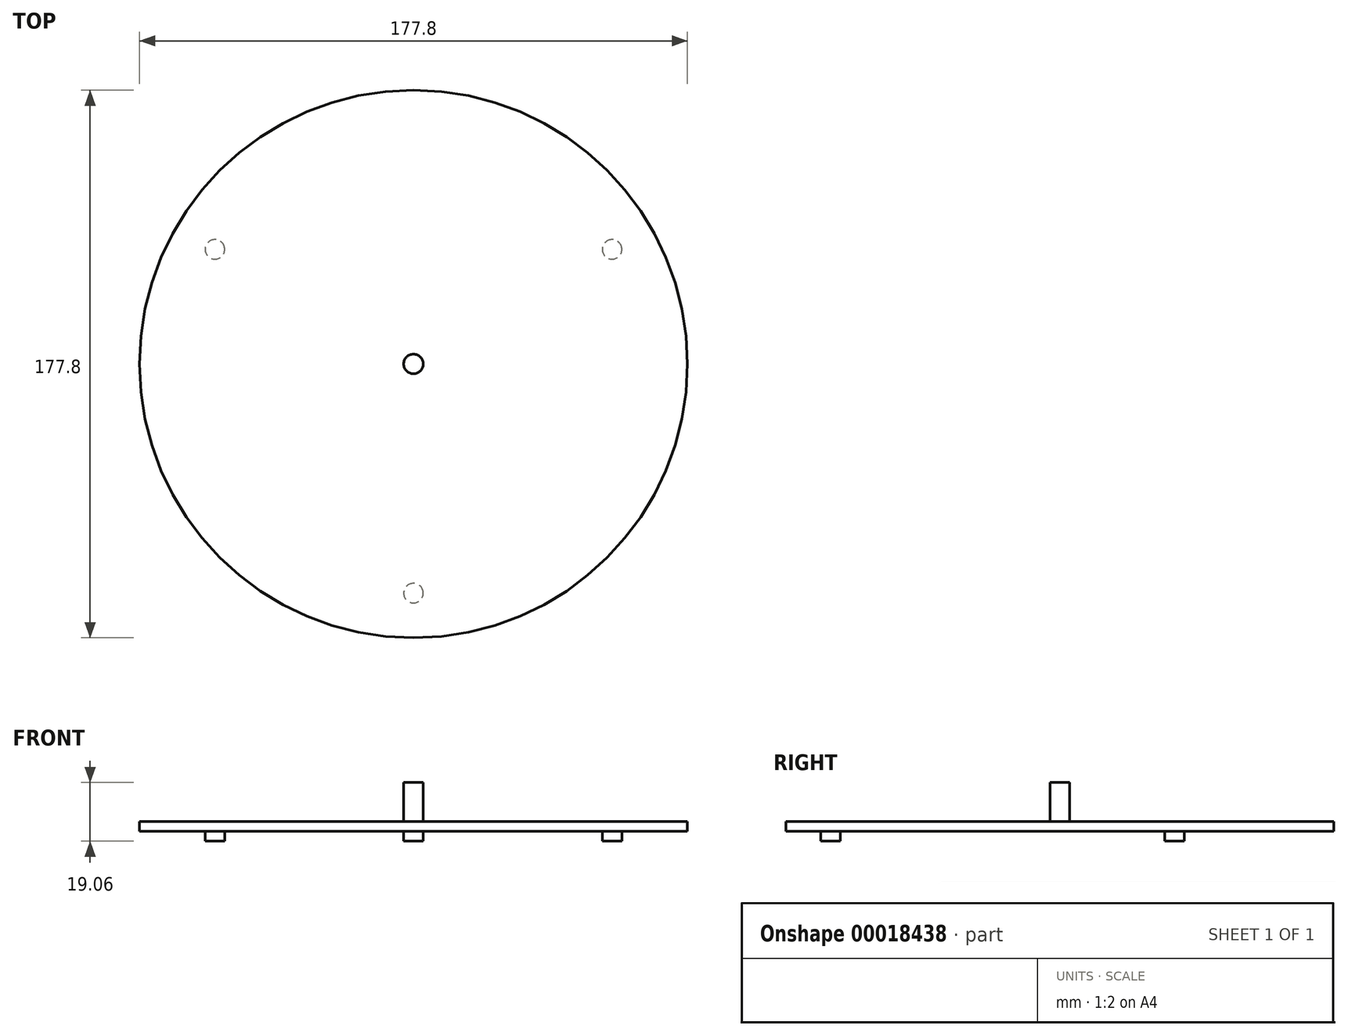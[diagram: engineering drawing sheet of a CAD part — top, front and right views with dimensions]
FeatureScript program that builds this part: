
annotation { "Feature Type Name" : "Feature", "Feature Type Description" : "" }
export const myFeature = defineFeature(function(context is Context, id is Id, definition is map)
    precondition{}
    {
        {
            var Q0;
            Q0=qCreatedBy(makeId("Top.planeOp"),FACE);
            var sketch = newSketch(context, id + "F0", { "sketchPlane" : qUnion([Q0])});
            skCircle(sketch, "E0", {"center": v(0, 0) * mm, "radius": 88.9 * mm});
            skSolve(sketch);
        }
        {
            var Q0;
            Q0=makeQuery(id+"F0.imprint","IMPRINT",FACE,{"disambiguationData":[TD([[makeQuery(id+"F0.imprint","IMPRINT",EDGE,{"derivedFrom":sQuery(id+"F0.wireOp",EDGE,"E0")}),1.0]])]});
            extrude(context, id + "F1", {"entities" : qUnion([Q0]), "depth" : 3.17 * mm});
        }
        {
            var Q0;
            Q0=makeQuery(id+"F1.opExtrude","CAP_FACE",FACE,{"disambiguationData":[OSD([sQuery(id+"F0.wireOp",EDGE,"E0")])],"isStart":false});
            var sketch = newSketch(context, id + "F2", { "sketchPlane" : qUnion([Q0])});
            skCircle(sketch, "E1", {"center": v(0, 0) * mm, "radius": 3.18 * mm});
            skSolve(sketch);
        }
        {
            var Q0;
            Q0=makeQuery(id+"F2.imprint","IMPRINT",FACE,{"disambiguationData":[TD([[makeQuery(id+"F2.imprint","IMPRINT",EDGE,{"derivedFrom":sQuery(id+"F2.wireOp",EDGE,"E1")}),1.0]])]});
            extrude(context, id + "F3", {"entities" : qUnion([Q0]), "operationType" : NewBodyOperationType.ADD, "depth" : 12.7 * mm});
        }
        {
            var Q0;
            Q0=makeQuery(id+"F1.opExtrude","CAP_FACE",FACE,{"disambiguationData":[OSD([sQuery(id+"F0.wireOp",EDGE,"E0")])],"isStart":false});
            var sketch = newSketch(context, id + "F4", { "sketchPlane" : qUnion([Q0])});
            skCircle(sketch, "E2.cCircle", {"center": v(0, 0) * mm, "radius": 74.4 * mm, "construction": true});
            skLineSegment(sketch, "E2.0", {"start": v(64.44, 37.2) * mm, "end": v(0, -74.4) * mm});
            skLineSegment(sketch, "E2.1", {"start": v(0, -74.4) * mm, "end": v(-64.44, 37.2) * mm});
            skLineSegment(sketch, "E2.2", {"start": v(-64.44, 37.2) * mm, "end": v(64.44, 37.2) * mm});
            skSolve(sketch);
        }
        {
            var Q0;
            Q0=makeQuery(id+"F4.imprint","IMPRINT",FACE,{"disambiguationData":[TD([[makeQuery(id+"F4.imprint","IMPRINT",EDGE,{"derivedFrom":sQuery(id+"F4.wireOp",EDGE,"E2.0")}),1.0]])]});
            var sketch = newSketch(context, id + "F5", { "sketchPlane" : qUnion([Q0])});
            skPoint(sketch, "E3.0", {"position": v(64.44, 37.2) * mm});
            skPoint(sketch, "E4.0", {"position": v(0, -74.4) * mm});
            skPoint(sketch, "E5.0", {"position": v(-64.44, 37.2) * mm});
            skCircle(sketch, "E6", {"center": v(64.44, 37.2) * mm, "radius": 3.18 * mm});
            skCircle(sketch, "E7", {"center": v(-64.44, 37.2) * mm, "radius": 3.18 * mm});
            skCircle(sketch, "E8", {"center": v(0, -74.4) * mm, "radius": 3.18 * mm});
            skSolve(sketch);
        }
        {
            var Q0;
            Q0 = qSketchRegion(id + "F5", true);
            extrude(context, id + "F6", {"entities" : qUnion([Q0]), "operationType" : NewBodyOperationType.ADD, "oppositeDirection" : true, "depth" : 6.35 * mm});
        }
    });
